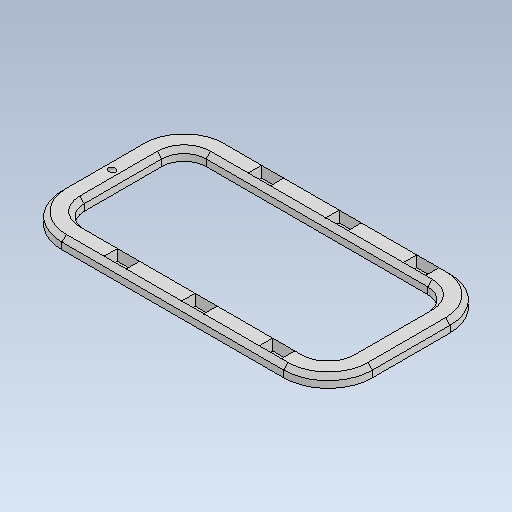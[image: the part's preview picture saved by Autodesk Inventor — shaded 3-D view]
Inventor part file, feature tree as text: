
AUTODESK INVENTOR PART (.ipt)
format: ipt  version: 2023 (Build 270158030, 158C)  size: 201,728 bytes
history: native  units: mm
features: other x4, sketch x2, sweep x1
ambient origin geometry x8: Origin, YZ Plane, XZ Plane, XY Plane, X Axis, Y Axis, Z Axis, Center Point
bodies: Body1 (feature_tree)
feature tree (7):
  other  "trebuchet-complete-parts.ipt"
  sweep  "Sweep1"
  other  "baseplate::trebuchet-complete-parts.ipt"
  other  "TaggingFeature1"
  sketch  "Sketch1"  dims[d0=10.0mm d1=2.5mm]
  sketch  "Sketch2"  dims[d2=1.0mm d3=37.5mm d4=37.5mm d5=0.174533mm d6=0.0mm]
  other  "baseplate"
